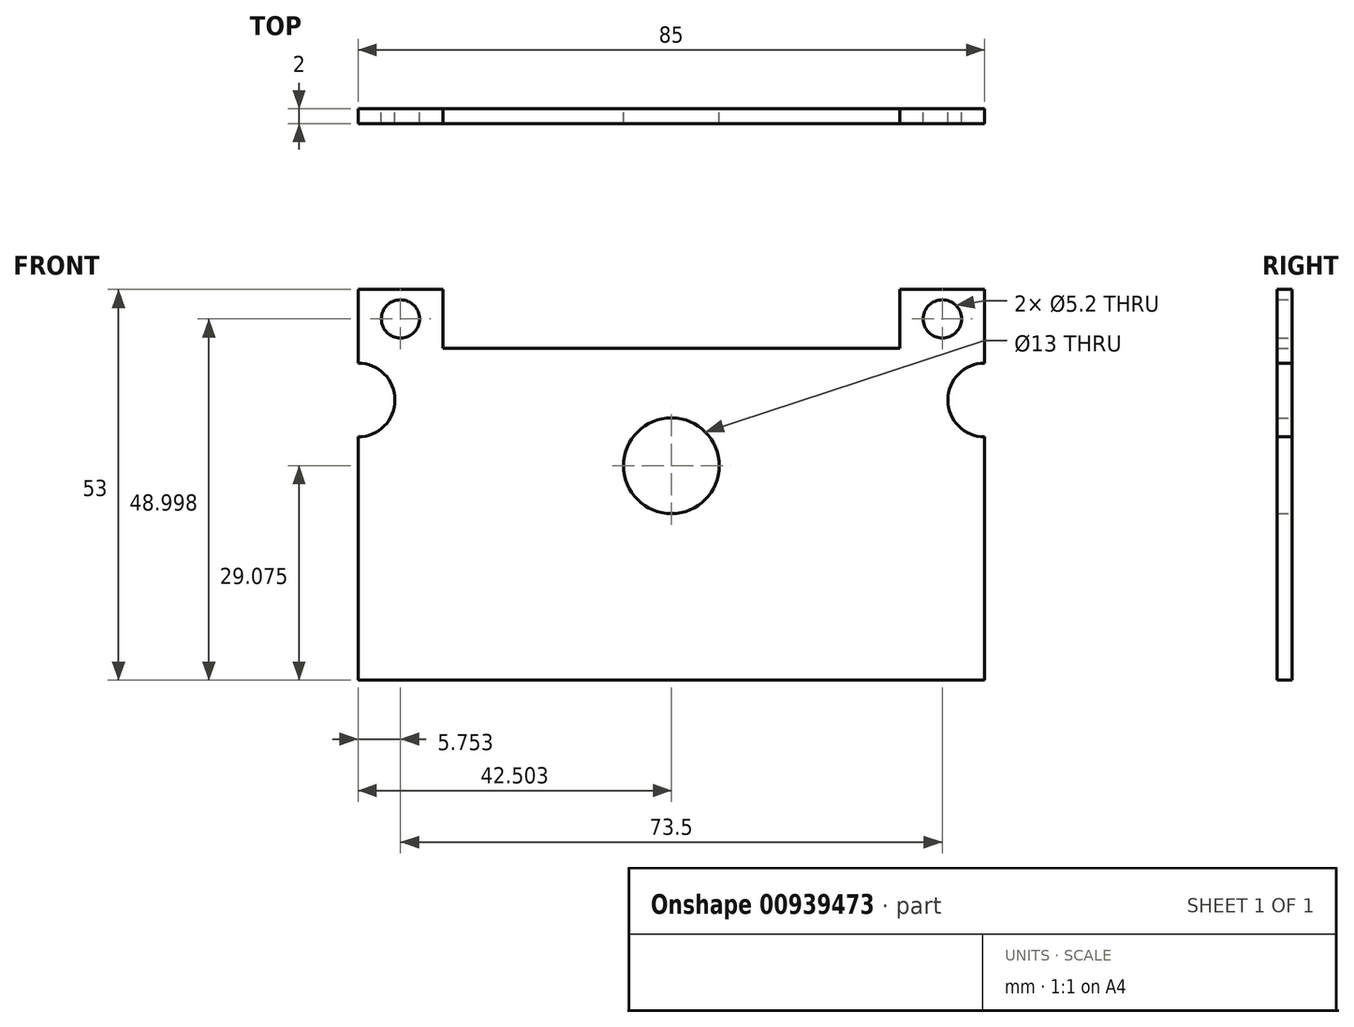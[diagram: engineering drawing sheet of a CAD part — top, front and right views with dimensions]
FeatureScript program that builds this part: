
annotation { "Feature Type Name" : "Feature", "Feature Type Description" : "" }
export const myFeature = defineFeature(function(context is Context, id is Id, definition is map)
    precondition{}
    {
        {
            var Q0;
            Q0=qCreatedBy(makeId("Front.planeOp"),FACE);
            var sketch = newSketch(context, id + "F0", { "sketchPlane" : qUnion([Q0])});
            skLineSegment(sketch, "E0.bottom", {"start": v(-45.77, 26.38) * mm, "end": v(16.23, 26.38) * mm});
            skLineSegment(sketch, "E0.top", {"start": v(-57.27, -18.62) * mm, "end": v(27.73, -18.62) * mm});
            skLineSegment(sketch, "E0.left", {"start": v(-57.27, 26.38) * mm, "end": v(-57.27, 24.38) * mm});
            skLineSegment(sketch, "E0.right", {"start": v(27.73, 26.38) * mm, "end": v(27.73, 24.38) * mm});
            skLineSegment(sketch, "E1.top", {"start": v(27.73, 34.38) * mm, "end": v(16.23, 34.38) * mm});
            skLineSegment(sketch, "E1.left", {"start": v(27.73, 26.38) * mm, "end": v(27.73, 34.38) * mm});
            skLineSegment(sketch, "E1.right", {"start": v(16.23, 26.38) * mm, "end": v(16.23, 34.38) * mm});
            skLineSegment(sketch, "E2.top", {"start": v(-57.27, 34.38) * mm, "end": v(-45.77, 34.38) * mm});
            skLineSegment(sketch, "E2.left", {"start": v(-57.27, 26.38) * mm, "end": v(-57.27, 34.38) * mm});
            skLineSegment(sketch, "E2.right", {"start": v(-45.77, 26.38) * mm, "end": v(-45.77, 34.38) * mm});
            skCircle(sketch, "E3", {"center": v(21.98, 30.38) * mm, "radius": 2.6 * mm});
            skPoint(sketch, "E3.centerSnap0", {"position": v(16.23, 30.38) * mm});
            skPoint(sketch, "E3.centerSnap1", {"position": v(21.98, 34.38) * mm});
            skCircle(sketch, "E4", {"center": v(-51.52, 30.38) * mm, "radius": 2.6 * mm});
            skPoint(sketch, "E4.centerSnap0", {"position": v(-57.27, 30.38) * mm});
            skPoint(sketch, "E4.centerSnap1", {"position": v(-51.52, 34.38) * mm});
            skCircle(sketch, "E5", {"center": v(-14.77, 10.45) * mm, "radius": 6.5 * mm});
            skPoint(sketch, "E5.centerSnap0", {"position": v(-14.77, -18.62) * mm});
            skArc(sketch, "E6", {"start": v(-57.27, 14.38) * mm, "mid": v(-52.27, 19.38) * mm, "end": v(-57.27, 24.38) * mm});
            skArc(sketch, "E7", {"start": v(27.73, 24.38) * mm, "mid": v(22.73, 19.38) * mm, "end": v(27.73, 14.38) * mm});
            skLineSegment(sketch, "E8.trimOffspring", {"start": v(-57.27, 14.38) * mm, "end": v(-57.27, -18.62) * mm});
            skLineSegment(sketch, "E9.trimOffspring", {"start": v(27.73, 14.38) * mm, "end": v(27.73, -18.62) * mm});
            skSolve(sketch);
        }
        {
            var Q0;
            Q0 = qSketchRegion(id + "F0", true);
            extrude(context, id + "F1", {"entities" : qUnion([Q0]), "depth" : 2 * mm, "offsetDistance" : 25 * mm});
        }
    });
